# Revit family: Furniture-Wall_Mount-Cabinet-KOHLER-Grooming-K-33695K_1
name_source: partatom
category: Casework
units: mm (PartAtom-declared; Revit-internal decimal feet)

## family parameters
Cut with Voids When Loaded = No
Host = Face
OmniClass Number = 23.21.23.17.11
OmniClass Title = Residential Cabinet
Room Calculation Point = No
Shared = No

## types (1)
- NA-Black
    ADA Compliant = No
    Apparent Load = 20 VA
    Assembly Code = E2010.30
    Construction Type = Wall Mount
    Date Modified = 05/29/2023
    Default Elevation = 60"
    Depth = 6 11/16"
    Description = 300 MM Showcase Side Cabinet Left Open
    Electrical Connector = Yes
    Electrical Note = One dedicated circuit required
    Finish = Kohler-Metal-NA-Black
    Hardware Included = No
    Height = 31 11/16"
    Manufacturer = Kohler Co.
    Master Format 2014 = 12 35 30.23
    Master Format 2014 Name = Bathroom Casework
    Material = Aluminium
    Model = K-33695K-L-NA
    Product Finish = Kohler-Metal-NA-Black
    Product Name = Grooming
    Type = 1
    URL = https://www.kohlerasiapacific.com
    Voltage = 240 V
    WaterSense Certified = No
    Wattage Comments = 20W
    Width = 11 13/16"

## geometry (parser evidence)
native form markers: Sweep x5
no freeform markers — native parametric forms only
